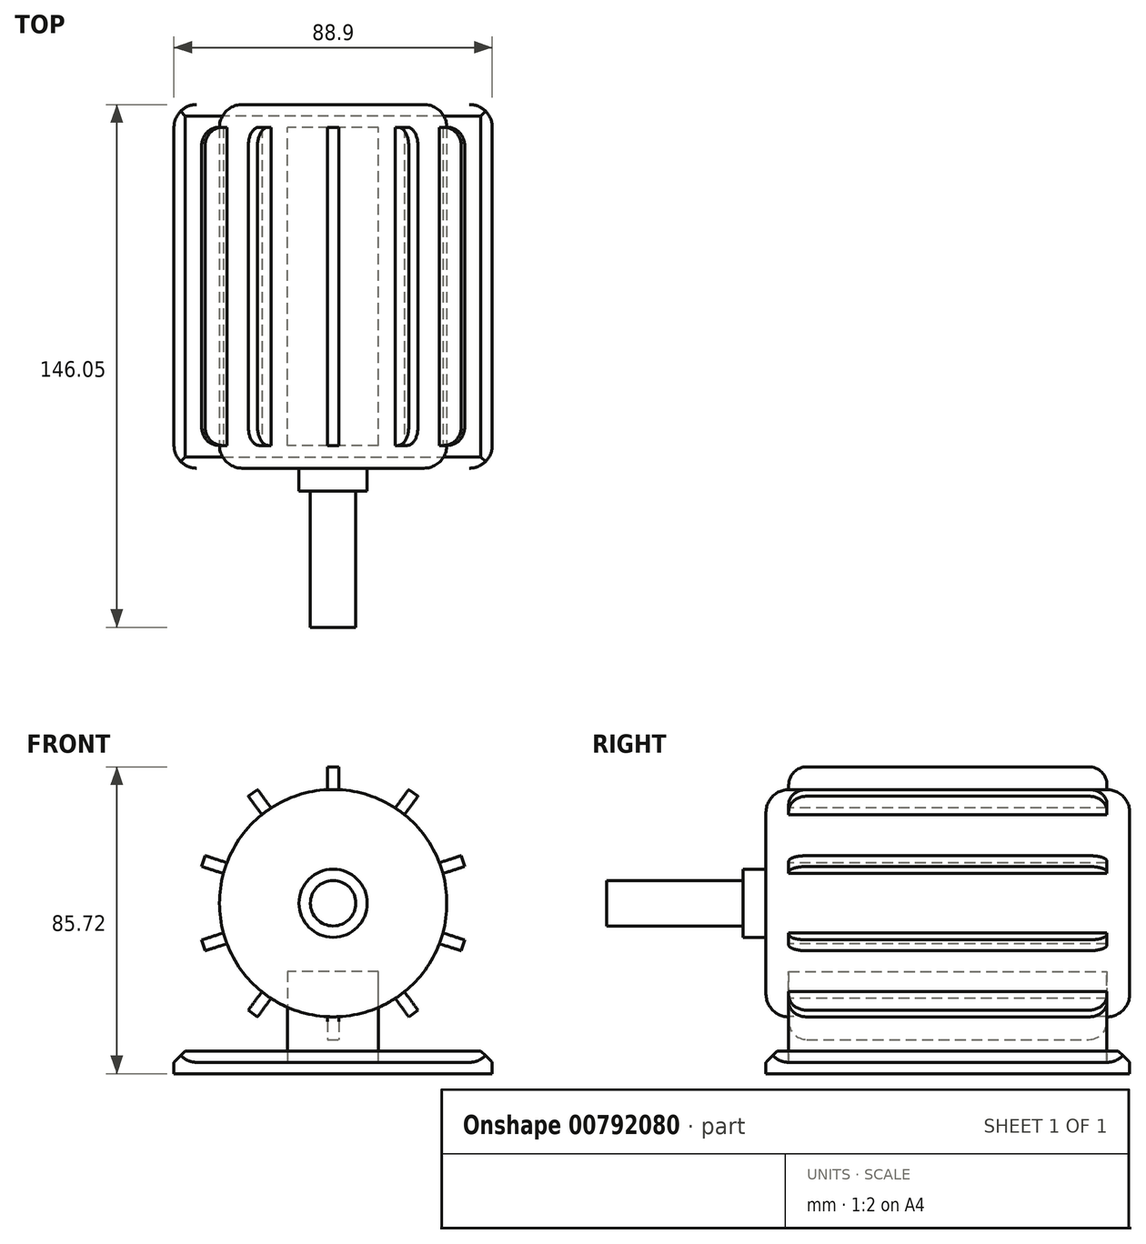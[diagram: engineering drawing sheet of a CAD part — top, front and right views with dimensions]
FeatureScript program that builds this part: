
annotation { "Feature Type Name" : "Feature", "Feature Type Description" : "" }
export const myFeature = defineFeature(function(context is Context, id is Id, definition is map)
    precondition{}
    {
        {
            var Q0;
            Q0=qCreatedBy(makeId("Front.planeOp"),FACE);
            var sketch = newSketch(context, id + "F0", { "sketchPlane" : qUnion([Q0])});
            skCircle(sketch, "E0", {"center": v(0, 44.45) * mm, "radius": 31.75 * mm});
            skLineSegment(sketch, "E1.bottom", {"start": v(44.45, 3.18) * mm, "end": v(-44.45, 3.18) * mm});
            skLineSegment(sketch, "E1.top", {"start": v(44.45, -3.17) * mm, "end": v(-44.45, -3.17) * mm});
            skLineSegment(sketch, "E1.left", {"start": v(44.45, 3.18) * mm, "end": v(44.45, -3.17) * mm});
            skLineSegment(sketch, "E1.right", {"start": v(-44.45, 3.18) * mm, "end": v(-44.45, -3.17) * mm});
            skPoint(sketch, "E1.middle", {"position": v(0, 0) * mm});
            skSolve(sketch);
        }
        {
            var Q0;
            Q0 = qSketchRegion(id + "F0", true);
            extrude(context, id + "F1", {"entities" : qUnion([Q0]), "oppositeDirection" : true, "depth" : 101.6 * mm, "offsetDistance" : 25.4 * mm});
        }
        {
            var Q0;
            Q0=makeQuery(id+"F1.opExtrude","CAP_EDGE",EDGE,{"disambiguationData":[OSD([sQuery(id+"F0.wireOp",EDGE,"E0")])],"isStart":true});
            var Q1;
            Q1=makeQuery(id+"F1.opExtrude","CAP_EDGE",EDGE,{"disambiguationData":[OSD([sQuery(id+"F0.wireOp",EDGE,"E0")])],"isStart":false});
            fillet(context, id + "F2", {"entities" : qUnion([Q0, Q1]), "radius" : 6.35 * mm, "tangentPropagation" : true, "allowEdgeOverflow" : false});
        }
        {
            var Q0;
            Q0=makeQuery(id+"F1.opExtrude","CAP_EDGE",EDGE,{"disambiguationData":[OSD([sQuery(id+"F0.wireOp",EDGE,"E1.bottom")])],"isStart":true});
            var Q1;
            Q1=makeQuery(id+"F1.opExtrude","SWEPT_EDGE",EDGE,{"disambiguationData":[OSD([sQuery(id+"F0.wireOp",EDGE,"E1.bottom"),sQuery(id+"F0.wireOp",EDGE,"E1.left")])]});
            var Q2;
            Q2=makeQuery(id+"F1.opExtrude","SWEPT_EDGE",EDGE,{"disambiguationData":[OSD([sQuery(id+"F0.wireOp",EDGE,"E1.bottom"),sQuery(id+"F0.wireOp",EDGE,"E1.right")])]});
            var Q3;
            Q3=makeQuery(id+"F1.opExtrude","CAP_EDGE",EDGE,{"disambiguationData":[OSD([sQuery(id+"F0.wireOp",EDGE,"E1.bottom")])],"isStart":false});
            chamfer(context, id + "F3", {"entities" : qUnion([Q0, Q1, Q2, Q3]), "width" : 3.17 * mm, "tangentPropagation" : true});
        }
        {
            var Q0;
            Q0=makeQuery(id+"F1.opExtrude","CAP_FACE",FACE,{"disambiguationData":[OSD([sQuery(id+"F0.wireOp",EDGE,"E0")])],"isStart":false});
            cPlane(context, id + "F4", {"entities" : qUnion([Q0]), "cplaneType" : CPlaneType.OFFSET, "offset" : 6.35 * mm, "oppositeDirection" : true, "width" : 152.4 * mm, "height" : 152.4 * mm});
        }
        {
            var Q0;
            Q0=qCreatedBy(id+"F4.planeOp",FACE);
            var sketch = newSketch(context, id + "F5", { "sketchPlane" : qUnion([Q0])});
            skLineSegment(sketch, "E2.bottom", {"start": v(1.59, 82.55) * mm, "end": v(-1.59, 82.55) * mm});
            skLineSegment(sketch, "E2.top", {"start": v(1.59, 6.35) * mm, "end": v(-1.59, 6.35) * mm});
            skLineSegment(sketch, "E2.left", {"start": v(1.59, 82.55) * mm, "end": v(1.59, 6.35) * mm});
            skLineSegment(sketch, "E2.right", {"start": v(-1.59, 82.55) * mm, "end": v(-1.59, 6.35) * mm});
            skPoint(sketch, "E2.middle", {"position": v(0, 44.45) * mm});
            skLineSegment(sketch, "E3.1.0", {"start": v(-35.74, 57.73) * mm, "end": v(36.73, 34.19) * mm});
            skLineSegment(sketch, "E3.1.1", {"start": v(-36.73, 54.71) * mm, "end": v(35.74, 31.17) * mm});
            skLineSegment(sketch, "E3.1.3", {"start": v(-35.74, 57.73) * mm, "end": v(-36.73, 54.71) * mm});
            skLineSegment(sketch, "E3.1.4", {"start": v(36.73, 34.19) * mm, "end": v(35.74, 31.17) * mm});
            skLineSegment(sketch, "E3.2.0", {"start": v(-23.68, 14.56) * mm, "end": v(21.11, 76.2) * mm});
            skLineSegment(sketch, "E3.2.1", {"start": v(-21.11, 12.7) * mm, "end": v(23.68, 74.34) * mm});
            skLineSegment(sketch, "E3.2.3", {"start": v(-23.68, 14.56) * mm, "end": v(-21.11, 12.7) * mm});
            skLineSegment(sketch, "E3.2.4", {"start": v(21.11, 76.2) * mm, "end": v(23.68, 74.34) * mm});
            skLineSegment(sketch, "E3.3.0", {"start": v(21.11, 12.7) * mm, "end": v(-23.68, 74.34) * mm});
            skLineSegment(sketch, "E3.3.1", {"start": v(23.68, 14.56) * mm, "end": v(-21.11, 76.2) * mm});
            skLineSegment(sketch, "E3.3.3", {"start": v(21.11, 12.7) * mm, "end": v(23.68, 14.56) * mm});
            skLineSegment(sketch, "E3.3.4", {"start": v(-23.68, 74.34) * mm, "end": v(-21.11, 76.2) * mm});
            skLineSegment(sketch, "E3.4.0", {"start": v(36.73, 54.71) * mm, "end": v(-35.74, 31.17) * mm});
            skLineSegment(sketch, "E3.4.1", {"start": v(35.74, 57.73) * mm, "end": v(-36.73, 34.19) * mm});
            skLineSegment(sketch, "E3.4.3", {"start": v(36.73, 54.71) * mm, "end": v(35.74, 57.73) * mm});
            skLineSegment(sketch, "E3.4.4", {"start": v(-35.74, 31.17) * mm, "end": v(-36.73, 34.19) * mm});
            skSolve(sketch);
        }
        {
            var Q0;
            Q0 = qSketchRegion(id + "F5", true);
            extrude(context, id + "F6", {"entities" : qUnion([Q0]), "operationType" : NewBodyOperationType.ADD, "oppositeDirection" : true, "depth" : 88.9 * mm, "offsetDistance" : 25.4 * mm});
        }
        {
            var Q0;
            Q0=makeQuery(id+"F6.opExtrude","CAP_EDGE",EDGE,{"disambiguationData":[OSD([sQuery(id+"F5.wireOp",EDGE,"E2.bottom")])],"isStart":true});
            var Q1;
            Q1=makeQuery(id+"F6.opExtrude","CAP_EDGE",EDGE,{"disambiguationData":[OSD([sQuery(id+"F5.wireOp",EDGE,"E3.2.4")])],"isStart":true});
            var Q2;
            Q2=makeQuery(id+"F6.opExtrude","CAP_EDGE",EDGE,{"disambiguationData":[OSD([sQuery(id+"F5.wireOp",EDGE,"E3.3.4")])],"isStart":true});
            var Q3;
            Q3=makeQuery(id+"F6.opExtrude","CAP_EDGE",EDGE,{"disambiguationData":[OSD([sQuery(id+"F5.wireOp",EDGE,"E3.1.3")])],"isStart":true});
            var Q4;
            Q4=makeQuery(id+"F6.opExtrude","CAP_EDGE",EDGE,{"disambiguationData":[OSD([sQuery(id+"F5.wireOp",EDGE,"E3.4.4")])],"isStart":true});
            var Q5;
            Q5=makeQuery(id+"F6.opExtrude","CAP_EDGE",EDGE,{"disambiguationData":[OSD([sQuery(id+"F5.wireOp",EDGE,"E3.2.3")])],"isStart":true});
            var Q6;
            Q6=makeQuery(id+"F6.opExtrude","CAP_EDGE",EDGE,{"disambiguationData":[OSD([sQuery(id+"F5.wireOp",EDGE,"E2.top")])],"isStart":true});
            var Q7;
            Q7=makeQuery(id+"F6.opExtrude","CAP_EDGE",EDGE,{"disambiguationData":[OSD([sQuery(id+"F5.wireOp",EDGE,"E3.3.3")])],"isStart":true});
            var Q8;
            Q8=makeQuery(id+"F6.opExtrude","CAP_EDGE",EDGE,{"disambiguationData":[OSD([sQuery(id+"F5.wireOp",EDGE,"E3.1.4")])],"isStart":true});
            var Q9;
            Q9=makeQuery(id+"F6.opExtrude","CAP_EDGE",EDGE,{"disambiguationData":[OSD([sQuery(id+"F5.wireOp",EDGE,"E3.4.3")])],"isStart":true});
            var Q10;
            Q10=makeQuery(id+"F6.opExtrude","CAP_EDGE",EDGE,{"disambiguationData":[OSD([sQuery(id+"F5.wireOp",EDGE,"E3.4.3")])],"isStart":false});
            var Q11;
            Q11=makeQuery(id+"F6.opExtrude","CAP_EDGE",EDGE,{"disambiguationData":[OSD([sQuery(id+"F5.wireOp",EDGE,"E3.1.4")])],"isStart":false});
            var Q12;
            Q12=makeQuery(id+"F6.opExtrude","CAP_EDGE",EDGE,{"disambiguationData":[OSD([sQuery(id+"F5.wireOp",EDGE,"E3.2.4")])],"isStart":false});
            var Q13;
            Q13=makeQuery(id+"F6.opExtrude","CAP_EDGE",EDGE,{"disambiguationData":[OSD([sQuery(id+"F5.wireOp",EDGE,"E2.bottom")])],"isStart":false});
            var Q14;
            Q14=makeQuery(id+"F6.opExtrude","CAP_EDGE",EDGE,{"disambiguationData":[OSD([sQuery(id+"F5.wireOp",EDGE,"E3.3.4")])],"isStart":false});
            var Q15;
            Q15=makeQuery(id+"F6.opExtrude","CAP_EDGE",EDGE,{"disambiguationData":[OSD([sQuery(id+"F5.wireOp",EDGE,"E3.1.3")])],"isStart":false});
            var Q16;
            Q16=makeQuery(id+"F6.opExtrude","CAP_EDGE",EDGE,{"disambiguationData":[OSD([sQuery(id+"F5.wireOp",EDGE,"E3.4.4")])],"isStart":false});
            var Q17;
            Q17=makeQuery(id+"F6.opExtrude","CAP_EDGE",EDGE,{"disambiguationData":[OSD([sQuery(id+"F5.wireOp",EDGE,"E3.2.3")])],"isStart":false});
            var Q18;
            Q18=makeQuery(id+"F6.opExtrude","CAP_EDGE",EDGE,{"disambiguationData":[OSD([sQuery(id+"F5.wireOp",EDGE,"E2.top")])],"isStart":false});
            var Q19;
            Q19=makeQuery(id+"F6.opExtrude","CAP_EDGE",EDGE,{"disambiguationData":[OSD([sQuery(id+"F5.wireOp",EDGE,"E3.3.3")])],"isStart":false});
            fillet(context, id + "F7", {"entities" : qUnion([Q0, Q1, Q2, Q3, Q4, Q5, Q6, Q7, Q8, Q9, Q10, Q11, Q12, Q13, Q14, Q15, Q16, Q17, Q18, Q19]), "radius" : 5.08 * mm, "tangentPropagation" : true, "allowEdgeOverflow" : false});
        }
        {
            var Q0;
            Q0=qCreatedBy(id+"F4.planeOp",FACE);
            var sketch = newSketch(context, id + "F8", { "sketchPlane" : qUnion([Q0])});
            skLineSegment(sketch, "E4.bottom", {"start": v(0, 0) * mm, "end": v(-12.7, 0) * mm});
            skLineSegment(sketch, "E4.top", {"start": v(0, 25.4) * mm, "end": v(-12.7, 25.4) * mm});
            skLineSegment(sketch, "E4.left", {"start": v(0, 0) * mm, "end": v(0, 25.4) * mm});
            skLineSegment(sketch, "E4.right", {"start": v(-12.7, 0) * mm, "end": v(-12.7, 25.4) * mm});
            skLineSegment(sketch, "E5.bottom", {"start": v(0, 25.4) * mm, "end": v(12.7, 25.4) * mm});
            skLineSegment(sketch, "E5.top", {"start": v(0, 0) * mm, "end": v(12.7, 0) * mm});
            skLineSegment(sketch, "E5.left", {"start": v(0, 25.4) * mm, "end": v(0, 0) * mm});
            skLineSegment(sketch, "E5.right", {"start": v(12.7, 25.4) * mm, "end": v(12.7, 0) * mm});
            skSolve(sketch);
        }
        {
            var Q0;
            Q0=makeQuery(id+"F8.imprint","IMPRINT",FACE,{"disambiguationData":[TD([[makeQuery(id+"F8.imprint","IMPRINT",EDGE,{"derivedFrom":sQuery(id+"F8.wireOp",EDGE,"E5.bottom")}),-1.0]])]});
            var Q1;
            Q1=makeQuery(id+"F8.imprint","IMPRINT",FACE,{"disambiguationData":[TD([[makeQuery(id+"F8.imprint","IMPRINT",EDGE,{"derivedFrom":sQuery(id+"F8.wireOp",EDGE,"E4.bottom")}),-1.0]])]});
            extrude(context, id + "F9", {"entities" : qUnion([Q0, Q1]), "oppositeDirection" : true, "depth" : 88.9 * mm, "offsetDistance" : 25.4 * mm});
        }
        {
            var Q0;
            Q0=makeQuery(id+"F1.opExtrude","CAP_EDGE",EDGE,{"disambiguationData":[OSD([sQuery(id+"F0.wireOp",EDGE,"E1.right")])],"isStart":false});
            var Q1;
            Q1=makeQuery(id+"F1.opExtrude","CAP_EDGE",EDGE,{"disambiguationData":[OSD([sQuery(id+"F0.wireOp",EDGE,"E1.left")])],"isStart":false});
            var Q2;
            Q2=makeQuery(id+"F1.opExtrude","CAP_EDGE",EDGE,{"disambiguationData":[OSD([sQuery(id+"F0.wireOp",EDGE,"E1.left")])],"isStart":true});
            var Q3;
            Q3=makeQuery(id+"F1.opExtrude","CAP_EDGE",EDGE,{"disambiguationData":[OSD([sQuery(id+"F0.wireOp",EDGE,"E1.right")])],"isStart":true});
            fillet(context, id + "F10", {"entities" : qUnion([Q0, Q1, Q2, Q3]), "radius" : 6.35 * mm, "tangentPropagation" : true, "allowEdgeOverflow" : false});
        }
        {
            var Q0;
            Q0=makeQuery(id+"F1.opExtrude","CAP_FACE",FACE,{"disambiguationData":[OSD([sQuery(id+"F0.wireOp",EDGE,"E0")])],"isStart":true});
            var sketch = newSketch(context, id + "F11", { "sketchPlane" : qUnion([Q0])});
            skCircle(sketch, "E6", {"center": v(0, 44.45) * mm, "radius": 9.53 * mm});
            skSolve(sketch);
        }
        {
            var Q0;
            Q0=makeQuery(id+"F11.imprint","IMPRINT",FACE,{"disambiguationData":[TD([[makeQuery(id+"F11.imprint","IMPRINT",EDGE,{"derivedFrom":sQuery(id+"F11.wireOp",EDGE,"E6")}),1.0]])]});
            extrude(context, id + "F12", {"entities" : qUnion([Q0]), "operationType" : NewBodyOperationType.ADD, "depth" : 6.35 * mm, "offsetDistance" : 25.4 * mm});
        }
        {
            var Q0;
            Q0=makeQuery(id+"F12.opExtrude","CAP_FACE",FACE,{"disambiguationData":[OSD([sQuery(id+"F11.wireOp",EDGE,"E6")])],"isStart":false});
            var sketch = newSketch(context, id + "F13", { "sketchPlane" : qUnion([Q0])});
            skCircle(sketch, "E7", {"center": v(0, 44.45) * mm, "radius": 6.35 * mm});
            skSolve(sketch);
        }
        {
            var Q0;
            Q0=makeQuery(id+"F13.imprint","IMPRINT",FACE,{"disambiguationData":[TD([[makeQuery(id+"F13.imprint","IMPRINT",EDGE,{"derivedFrom":sQuery(id+"F13.wireOp",EDGE,"E7")}),1.0]])]});
            extrude(context, id + "F14", {"entities" : qUnion([Q0]), "operationType" : NewBodyOperationType.ADD, "depth" : 38.1 * mm, "offsetDistance" : 25.4 * mm});
        }
    });
